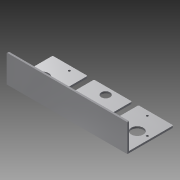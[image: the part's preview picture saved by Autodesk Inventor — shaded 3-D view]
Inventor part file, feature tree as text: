
AUTODESK INVENTOR PART (.ipt)
format: ipt  version: 2015 (Build 190159000, 159)  size: 193,536 bytes
history: native  units: mm
features: extrude x9, sketch x9, fillet x3, hole x2
ambient origin geometry x8: Origin, YZ Plane, XZ Plane, XY Plane, X Axis, Y Axis, Z Axis, Center Point
bodies: Solid1 (feature_tree)
feature tree (23):
  extrude  "Extrusion1"  Depth=7.0mm
  sketch  "Sketch2"  dims[d18=7.0mm]
  hole  "Hole1"  [1 undecoded]
  hole  "Hole2"  [1 undecoded]
  extrude  "Extrusion3"  Depth=3.5mm
  extrude  "Extrusion4"  Depth=7.0mm
  extrude  "Extrusion6"  Depth=2.0mm
  extrude  "Extrusion7"  TaperAngle=180.0deg  [1 undecoded]
  extrude  "Extrusion8"  Depth=1.0mm
  extrude  "Extrusion9"  Depth=1.0mm
  fillet  "Fillet1"  Radius=2.4mm
  fillet  "Fillet2"  Radius=2.4mm
  extrude  "Extrusion10"  Depth=1.0mm
  extrude  "Extrusion11"  Depth=1.0mm
  fillet  "Fillet3"  Radius=2.0mm
  sketch  "Sketch1"  dims[d11=131.0mm d12=0.0mm d17=7.0mm]
  sketch  "Sketch3"  dims[d19=7.0mm d20=6.0mm d21=4.0mm d22=2.0mm d23=90.0deg d24=2.0mm d25=0.0mm d26=51.3mm]
  sketch  "Sketch7"  dims[d27=51.3mm d28=19.0mm]
  sketch  "Sketch8"  dims[d29=3.5mm d30=3.5mm]
  sketch  "Sketch9"  dims[d31=3.5mm d32=6.0mm d33=4.0mm d34=2.0mm d35=90.0deg d36=2.0mm d37=0.0mm d89=7.0mm]
  sketch  "Sketch11"  dims[d90=2.0mm d91=0.0mm d96=31.0mm]
  sketch  "Sketch12"  dims[d97=25.0mm d98=180.0deg]
  sketch  "Sketch14"  dims[d99=50.0mm d100=2.4mm d101=2.4mm d104=2.4mm d105=2.4mm d106=2.4mm d107=2.4mm d108=2.0mm d109=0.0mm d112=2.0mm d113=0.0mm d114=2.0mm d115=0.0mm d116=13.0mm d117=13.0mm d118=2.0mm d119=0.0mm d125=2.0mm d126=0.0mm d127=1.0mm d128=1.0mm d129=8.0mm d130=9.5mm d131=2.0mm d132=0.0mm d133=18.0mm d134=0.0mm d135=1.0mm]
note: 3 required parameter values undecoded (feature->parameter linkage not recoverable at this tier; creation-order binding heuristic only, values carry confidence <= 0.55)
